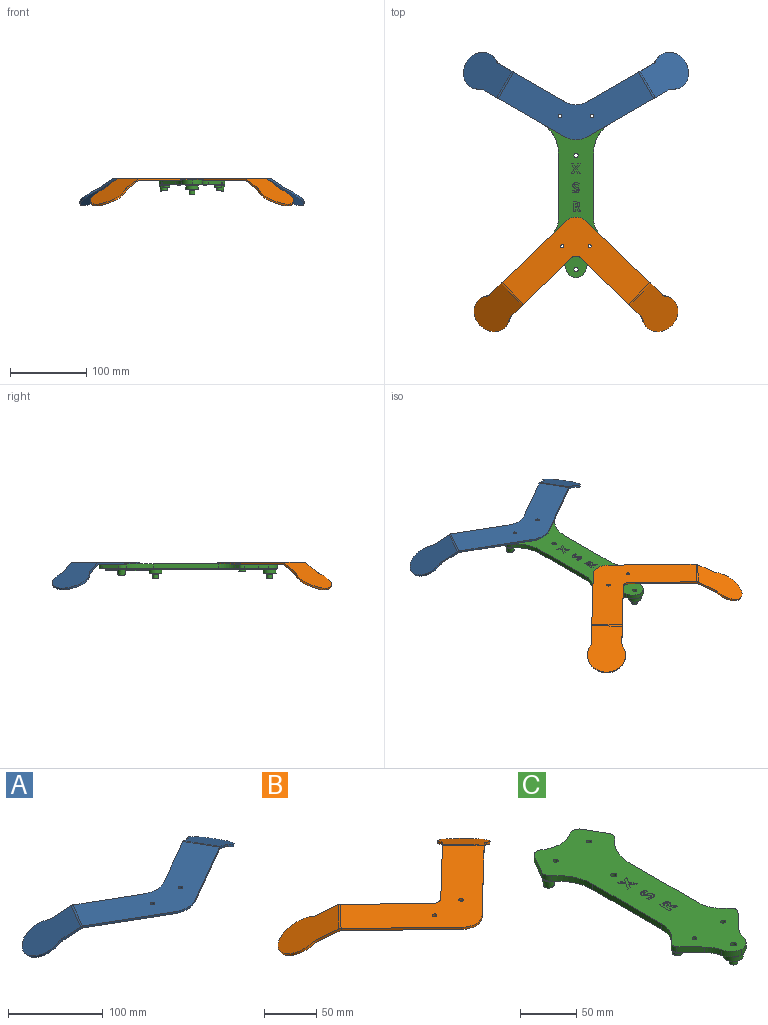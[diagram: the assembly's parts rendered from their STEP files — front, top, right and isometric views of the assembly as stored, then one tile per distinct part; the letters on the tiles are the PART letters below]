
ASSEMBLY  parts=3 mates=2
PART A: 32 faces, bbox 296.1x115.1x36.2 mm
  f0: plane 67.21x38.81mm, normal (0.5,0.87,0), area 194mm2, adj f6,f7,f9,f29
  f1: plane 67.21x38.81mm, normal (-0.5,0.87,0), area 194mm2, adj f6,f7,f9,f17
  f2: plane 87.21x50.35mm, normal (0.5,-0.87,0), area 251.8mm2, adj f6,f7,f8,f18
  f3: cylinder r=2.15mm len=4.3mm, axis (0,0,1), area 33.8mm2, adj f6,f7
  f4: cylinder r=2.15mm len=4.3mm, axis (0,0,1), area 33.8mm2, adj f6,f7
  f5: plane 87.21x50.35mm, normal (-0.5,-0.87,0), area 251.8mm2, adj f6,f7,f8,f28
  f6: plane 204.42x89.01mm, normal (0,0,-1), area 8489.2mm2, adj f0,f1,f2,f3,f4,f5,f8,f9
  f7: plane 204.42x89.01mm, normal (0,0,1), area 8489.2mm2, adj f0,f1,f2,f3,f4,f5,f8,f9
  f8: cylinder r=30mm len=30mm, axis (0,0,1), area 78.5mm2, adj f2,f5,f6,f7
  f9: cylinder r=30mm len=30mm, axis (0,0,-1), area 78.5mm2, adj f0,f1,f6,f7
  f10: plane 18.92x14.06mm, normal (0.5,-0.87,0), area 59.4mm2, adj f13,f14,f15,f18
  f11: plane 18.92x14.06mm, normal (-0.5,0.87,0), area 59.4mm2, adj f13,f14,f16,f17
  f12: cylinder r=25mm len=49.04mm, axis (-0.43,-0.25,-0.87), area 264mm2, adj f13,f14,f15,f16
  f13: plane 63.89x59.63mm, normal (-0.43,-0.25,-0.87), area 2757.9mm2, adj f10,f11,f12,f15,f16,f20
  f14: plane 63.89x59.63mm, normal (0.43,0.25,0.87), area 2757.9mm2, adj f10,f11,f12,f15,f16,f19
  f15: cylinder r=10mm len=5.66mm, axis (-0.43,-0.25,-0.87), area 13.5mm2, adj f10,f12,f13,f14
  f16: cylinder r=10mm len=4.74mm, axis (-0.43,-0.25,-0.87), area 13.5mm2, adj f11,f12,f13,f14
  f17: plane 2.76x1.93mm, normal (-0.5,0.87,0), area 4.2mm2, adj f1,f11,f19,f20
  f18: plane 2.76x1.93mm, normal (0.5,-0.87,0), area 4.2mm2, adj f2,f10,f19,f20
  f19: cylinder r=4.45mm len=35.75mm, axis (-0.5,0.87,0), area 93.2mm2, adj f7,f14,f17,f18
  f20: cylinder r=1.95mm len=35.13mm, axis (-0.5,0.87,0), area 40.8mm2, adj f6,f13,f17,f18
  f21: plane 18.92x14.06mm, normal (0.5,0.87,0), area 59.4mm2, adj f24,f25,f26,f29
  f22: plane 18.92x14.06mm, normal (-0.5,-0.87,0), area 59.4mm2, adj f24,f25,f27,f28
  f23: cylinder r=25mm len=49.04mm, axis (0.43,-0.25,-0.87), area 264mm2, adj f24,f25,f26,f27
  f24: plane 63.89x59.63mm, normal (0.43,-0.25,-0.87), area 2757.9mm2, adj f21,f22,f23,f26,f27,f31
  f25: plane 63.89x59.63mm, normal (-0.43,0.25,0.87), area 2757.9mm2, adj f21,f22,f23,f26,f27,f30
  f26: cylinder r=10mm len=4.74mm, axis (0.43,-0.25,-0.87), area 13.5mm2, adj f21,f23,f24,f25
  f27: cylinder r=10mm len=5.66mm, axis (0.43,-0.25,-0.87), area 13.5mm2, adj f22,f23,f24,f25
  f28: plane 2.76x1.93mm, normal (-0.5,-0.87,0), area 4.2mm2, adj f5,f22,f30,f31
  f29: plane 2.76x1.93mm, normal (0.5,0.87,0), area 4.2mm2, adj f0,f21,f30,f31
  f30: cylinder r=4.45mm len=35.75mm, axis (-0.5,-0.87,0), area 93.2mm2, adj f7,f25,f28,f29
  f31: cylinder r=1.95mm len=35.13mm, axis (-0.5,-0.87,0), area 40.8mm2, adj f6,f24,f28,f29
PART B: 32 faces, bbox 268.1x150.4x36.2 mm
  f0: plane 63.62x61.43mm, normal (0.69,0.72,0), area 221.1mm2, adj f6,f7,f9,f29
  f1: plane 63.62x61.43mm, normal (-0.69,0.72,0), area 221.1mm2, adj f6,f7,f9,f17
  f2: plane 83.07x80.22mm, normal (0.69,-0.72,0), area 288.7mm2, adj f6,f7,f8,f18
  f3: cylinder r=2.15mm len=4.3mm, axis (0,0,1), area 33.8mm2, adj f6,f7
  f4: cylinder r=2.15mm len=4.3mm, axis (0,0,1), area 33.8mm2, adj f6,f7
  f5: plane 83.07x80.22mm, normal (-0.69,-0.72,0), area 288.7mm2, adj f6,f7,f8,f28
  f6: plane 193.92x114.6mm, normal (0,0,-1), area 9142.7mm2, adj f0,f1,f2,f3,f4,f5,f8,f9
  f7: plane 193.92x114.6mm, normal (0,0,1), area 9142.7mm2, adj f0,f1,f2,f3,f4,f5,f8,f9
  f8: cylinder r=20mm len=27.79mm, axis (0,0,1), area 76.8mm2, adj f2,f5,f6,f7
  f9: cylinder r=8mm len=11.11mm, axis (0,0,-1), area 30.7mm2, adj f0,f1,f6,f7
  f10: plane 15.71x15.17mm, normal (0.69,-0.72,0), area 59.4mm2, adj f13,f14,f15,f18
  f11: plane 15.71x15.17mm, normal (-0.69,0.72,0), area 59.4mm2, adj f13,f14,f16,f17
  f12: cylinder r=25mm len=47.47mm, axis (-0.36,-0.35,-0.87), area 264mm2, adj f13,f14,f15,f16
  f13: plane 63.27x62.98mm, normal (-0.36,-0.35,-0.87), area 2757.9mm2, adj f10,f11,f12,f15,f16,f20
  f14: plane 63.27x62.98mm, normal (0.36,0.35,0.87), area 2757.9mm2, adj f10,f11,f12,f15,f16,f19
  f15: cylinder r=10mm len=5.1mm, axis (-0.36,-0.35,-0.87), area 13.5mm2, adj f10,f12,f13,f14
  f16: cylinder r=10mm len=4.99mm, axis (-0.36,-0.35,-0.87), area 13.5mm2, adj f11,f12,f13,f14
  f17: plane 2.76x1.6mm, normal (-0.69,0.72,0), area 4.2mm2, adj f1,f11,f19,f20
  f18: plane 2.76x1.6mm, normal (0.69,-0.72,0), area 4.2mm2, adj f2,f10,f19,f20
  f19: cylinder r=4.45mm len=30.32mm, axis (-0.69,0.72,0), area 93.2mm2, adj f7,f14,f17,f18
  f20: cylinder r=1.95mm len=29.45mm, axis (-0.69,0.72,0), area 40.8mm2, adj f6,f13,f17,f18
  f21: plane 15.71x15.17mm, normal (0.69,0.72,0), area 59.4mm2, adj f24,f25,f26,f29
  f22: plane 15.71x15.17mm, normal (-0.69,-0.72,0), area 59.4mm2, adj f24,f25,f27,f28
  f23: cylinder r=25mm len=47.47mm, axis (0.36,-0.35,-0.87), area 264mm2, adj f24,f25,f26,f27
  f24: plane 63.27x62.98mm, normal (0.36,-0.35,-0.87), area 2757.9mm2, adj f21,f22,f23,f26,f27,f31
  f25: plane 63.27x62.98mm, normal (-0.36,0.35,0.87), area 2757.9mm2, adj f21,f22,f23,f26,f27,f30
  f26: cylinder r=10mm len=4.99mm, axis (0.36,-0.35,-0.87), area 13.5mm2, adj f21,f23,f24,f25
  f27: cylinder r=10mm len=5.1mm, axis (0.36,-0.35,-0.87), area 13.5mm2, adj f22,f23,f24,f25
  f28: plane 2.76x1.6mm, normal (-0.69,-0.72,0), area 4.2mm2, adj f5,f22,f30,f31
  f29: plane 2.76x1.6mm, normal (0.69,0.72,0), area 4.2mm2, adj f0,f21,f30,f31
  f30: cylinder r=4.45mm len=30.32mm, axis (-0.69,-0.72,0), area 93.2mm2, adj f7,f25,f28,f29
  f31: cylinder r=1.95mm len=29.45mm, axis (-0.69,-0.72,0), area 40.8mm2, adj f6,f24,f28,f29
PART C: 179 faces, bbox 86x237.1x20.2 mm
  f0: cylinder r=3.8mm len=8.7mm, axis (0.17,0,-0.98), area 167.1mm2, adj f88,f178
  f1: cylinder r=3.8mm len=8.7mm, axis (-0.17,0,-0.98), area 167.1mm2, adj f90,f177
  f2: plane 234.51x85.78mm, normal (0,0,1), area 11832.9mm2, adj f4,f5,f6,f7,f8,f9,f10,f11
  f3: plane 234.51x81.33mm, normal (0,0,-1), area 6895.4mm2, adj f8,f9,f10,f11,f12,f13,f14,f15
  f4: cylinder r=2.2mm len=4.4mm, axis (0,0,1), area 48.4mm2, adj f2,f54
  f5: cylinder r=2.2mm len=4.4mm, axis (0,0,1), area 48.4mm2, adj f2,f52
  f6: cylinder r=2.2mm len=4.4mm, axis (0,0,1), area 48.4mm2, adj f2,f50
  f7: cylinder r=2.2mm len=4.4mm, axis (0,0,1), area 48.4mm2, adj f2,f48
  f8: plane 21.39x12.39mm, normal (0.87,0.5,0), area 147.6mm2, adj f2,f3,f81,f84,f92
  f9: plane 6x3.59mm, normal (-0.5,0.87,0), area 24.9mm2, adj f2,f3,f38,f81
  f10: plane 6x3.59mm, normal (0.5,0.87,0), area 24.9mm2, adj f2,f3,f38,f82
  f11: plane 21.39x12.38mm, normal (-0.87,0.5,0), area 147.6mm2, adj f2,f3,f82,f83,f99
  f12: plane 86.29x6mm, normal (-1,0,0), area 517.7mm2, adj f2,f3,f43,f79
  f13: plane 6.25x6.19mm, normal (-0.69,0.72,0), area 49.6mm2, adj f2,f3,f43,f45,f100
  f14: plane 17.96x17.35mm, normal (-0.72,-0.69,0), area 147.7mm2, adj f2,f3,f41,f45,f103
  f15: plane 17.96x17.35mm, normal (0.72,-0.69,0), area 147.7mm2, adj f2,f3,f42,f46,f104
  f16: plane 6.25x6.19mm, normal (0.69,0.72,0), area 49.6mm2, adj f2,f3,f44,f46,f107
  f17: plane 86.29x6mm, normal (1,0,0), area 517.7mm2, adj f2,f3,f44,f80
  f18: cylinder r=8.5mm len=17mm, axis (0,0,1), area 263mm2, adj f19,f56,f68,f74,f85,f86,f87
  f19: plane 17x17mm, normal (0,0,-1), area 170.2mm2, adj f18,f175
  f20: cylinder r=8.5mm len=17mm, axis (0,0,1), area 267mm2, adj f21,f56,f73
  f21: plane 17x17mm, normal (0,0,-1), area 170.2mm2, adj f20,f176
  f22: cylinder r=2.75mm len=20mm, axis (0,0,1), area 345.6mm2, adj f2,f172
  f23: cylinder r=2.75mm len=20mm, axis (0,0,1), area 345.6mm2, adj f2,f174
  f24: plane 150x3mm, normal (0,0,-1), area 450mm2, adj f28,f29,f34,f35
  f25: plane 150x3mm, normal (0,0,-1), area 450mm2, adj f26,f27,f36,f37
  f26: plane 150.21x0.64mm, normal (-0.95,0,-0.32), area 100mm2, adj f25,f33,f36,f37
  f27: plane 150.21x0.64mm, normal (0.95,0,-0.32), area 100mm2, adj f25,f32,f36,f37
  f28: plane 150.21x0.64mm, normal (-0.95,0,-0.32), area 100mm2, adj f24,f31,f34,f35
  f29: plane 150.21x0.64mm, normal (0.95,0,-0.32), area 100mm2, adj f24,f30,f34,f35
  f30: cylinder r=2mm len=154mm, axis (0,1,0), area 380mm2, adj f3,f29,f34,f35
  f31: cylinder r=2mm len=154mm, axis (0,1,0), area 380mm2, adj f3,f28,f34,f35
  f32: cylinder r=2mm len=154mm, axis (0,1,0), area 380mm2, adj f3,f27,f36,f37
  f33: cylinder r=2mm len=154mm, axis (0,1,0), area 380mm2, adj f3,f26,f36,f37
  f34: cylinder r=2mm len=7.22mm, axis (-1,0,0), area 15.4mm2, adj f3,f24,f28,f29,f30,f31
  f35: cylinder r=2mm len=7.22mm, axis (1,0,0), area 15.4mm2, adj f3,f24,f28,f29,f30,f31
  f36: cylinder r=2mm len=7.22mm, axis (-1,0,0), area 15.4mm2, adj f3,f25,f26,f27,f32,f33
  f37: cylinder r=2mm len=7.22mm, axis (1,0,0), area 15.4mm2, adj f3,f25,f26,f27,f32,f33
  f38: cylinder r=30mm len=30mm, axis (0,0,-1), area 188.5mm2, adj f2,f3,f9,f10
  f39: cylinder r=15mm len=13.51mm, axis (0,0,-1), area 113.9mm2, adj f2,f3,f40,f42
  f40: cylinder r=15mm len=13.51mm, axis (0,0,-1), area 113.9mm2, adj f2,f3,f39,f41
  f41: cylinder r=30mm len=13.92mm, axis (0,0,-1), area 96.3mm2, adj f2,f3,f14,f40
  f42: cylinder r=30mm len=13.92mm, axis (0,0,-1), area 96.3mm2, adj f2,f3,f15,f39
  f43: cylinder r=30mm len=21.58mm, axis (0,0,1), area 144.5mm2, adj f2,f3,f12,f13
  f44: cylinder r=30mm len=21.58mm, axis (0,0,1), area 144.5mm2, adj f2,f3,f16,f17
  f45: cylinder r=5mm len=7.07mm, axis (0,0,-1), area 47.1mm2, adj f2,f13,f14,f102
  f46: cylinder r=5mm len=7.07mm, axis (0,0,-1), area 47.1mm2, adj f2,f15,f16,f106
  f47: cylinder r=5mm len=10mm, axis (0,0,-1), area 78.5mm2, adj f3,f48
  f48: plane 10x10mm, normal (0,0,-1), area 63.3mm2, adj f7,f47
  f49: cylinder r=5mm len=10mm, axis (0,0,-1), area 78.5mm2, adj f3,f50
  f50: plane 10x10mm, normal (0,0,-1), area 63.3mm2, adj f6,f49
  f51: cylinder r=5mm len=10mm, axis (0,0,-1), area 78.5mm2, adj f3,f52
  f52: plane 10x10mm, normal (0,0,-1), area 63.3mm2, adj f5,f51
  f53: cylinder r=5mm len=10mm, axis (0,0,-1), area 78.5mm2, adj f3,f54
  f54: plane 10x10mm, normal (0,0,-1), area 63.3mm2, adj f4,f53
  f55: plane 4.54x2mm, normal (0,1,0), area 8.2mm2, adj f67,f72,f78,f85,f86,f87
  f56: plane 133.48x9.6mm, normal (0,0,-1), area 522.4mm2, adj f18,f20,f65,f69,f70,f71,f75,f76
  f57: cylinder r=3.8mm len=7.6mm, axis (0,0,1), area 95.5mm2, adj f59,f60
  f58: cylinder r=4.8mm len=9.6mm, axis (0,0,1), area 65.6mm2, adj f59,f104,f105,f106,f107
  f59: plane 9.6x9.6mm, normal (0,0,-1), area 27mm2, adj f57,f58
  f60: plane 7.6x7.6mm, normal (0,0,-1), area 45.4mm2, adj f57
  f61: cylinder r=3.8mm len=7.6mm, axis (0,0,1), area 95.5mm2, adj f63,f64
  f62: cylinder r=4.8mm len=9.6mm, axis (0,0,1), area 65.6mm2, adj f63,f100,f101,f102,f103
  f63: plane 9.6x9.6mm, normal (0,0,-1), area 27mm2, adj f61,f62
  f64: plane 7.6x7.6mm, normal (0,0,-1), area 45.4mm2, adj f61
  f65: cylinder r=3.8mm len=7.6mm, axis (0,0,1), area 47.8mm2, adj f56,f66
  f66: plane 7.6x7.6mm, normal (0,0,-1), area 45.4mm2, adj f65
  f67: cylinder r=2mm len=58.39mm, axis (0,1,0), area 179.1mm2, adj f3,f55,f68,f78,f86
  f68: torus R=10.5mm, axis (0,0,1), area 72.7mm2, adj f3,f18,f67,f69
  f69: cylinder r=2mm len=44.63mm, axis (0,1,0), area 136.1mm2, adj f3,f56,f68,f70
  f70: torus R=6.8mm, axis (0,0,1), area 35.9mm2, adj f3,f56,f69,f71
  f71: cylinder r=2mm len=80.13mm, axis (0,1,0), area 247.7mm2, adj f3,f56,f70,f73
  f72: cylinder r=2mm len=58.39mm, axis (0,-1,0), area 179.1mm2, adj f3,f55,f74,f78,f85
  f73: torus R=10.5mm, axis (0,0,1), area 163.7mm2, adj f3,f20,f71,f75
  f74: torus R=10.5mm, axis (0,0,1), area 72.7mm2, adj f3,f18,f72,f76
  f75: cylinder r=2mm len=80.13mm, axis (0,-1,0), area 247.7mm2, adj f3,f56,f73,f77
  f76: cylinder r=2mm len=44.63mm, axis (0,-1,0), area 136.1mm2, adj f3,f56,f74,f77
  f77: torus R=6.8mm, axis (0,0,1), area 35.9mm2, adj f3,f56,f75,f76
  f78: cylinder r=1mm len=8mm, axis (-1,0,0), area 9.8mm2, adj f3,f55,f67,f72
  f79: cylinder r=45mm len=35.14mm, axis (0,0,-1), area 241.9mm2, adj f2,f3,f12,f83,f96
  f80: cylinder r=45mm len=35.14mm, axis (0,0,-1), area 241.9mm2, adj f2,f3,f17,f84,f95
  f81: cylinder r=8mm len=10.93mm, axis (0,0,-1), area 75.4mm2, adj f2,f3,f8,f9
  f82: cylinder r=8mm len=10.93mm, axis (0,0,-1), area 75.4mm2, adj f2,f3,f10,f11
  f83: cylinder r=8mm len=10.25mm, axis (0,0,-1), area 68.1mm2, adj f2,f11,f79,f98
  f84: cylinder r=8mm len=10.25mm, axis (0,0,-1), area 68.1mm2, adj f2,f8,f80,f94
  f85: plane 57.39x1mm, normal (-1,0,0), area 57.4mm2, adj f18,f55,f72,f87
  f86: plane 57.39x1mm, normal (1,0,0), area 57.4mm2, adj f18,f55,f67,f87
  f87: plane 57.39x4mm, normal (0,0,-1), area 228.9mm2, adj f18,f55,f85,f86
  f88: plane 9.6x9.46mm, normal (0.17,0,-0.98), area 27mm2, adj f0,f89
  f89: bspline ~10.99x9.6mm, area 198.9mm2, adj f88,f96,f97,f98,f99
  f90: plane 9.6x9.46mm, normal (-0.17,0,-0.98), area 27mm2, adj f1,f91
  f91: bspline ~10.99x9.6mm, area 197mm2, adj f90,f92,f93,f94,f95
  f92: bspline ~3.38x2.53mm, area 4.4mm2, adj f8,f91,f93,f94
  f93: bspline ~13.61x10.48mm, area 70.5mm2, adj f3,f91,f92,f95
  f94: bspline ~11.34x4.44mm, area 13.8mm2, adj f84,f91,f92,f95
  f95: bspline ~2.51x2.1mm, area 1.6mm2, adj f80,f91,f93,f94
  f96: bspline ~2.28x1.98mm, area 1.6mm2, adj f79,f89,f97,f98
  f97: bspline ~13.6x9.87mm, area 70.5mm2, adj f3,f89,f96,f99
  f98: bspline ~11.13x4.2mm, area 13.8mm2, adj f83,f89,f96,f99
  f99: bspline ~3.62x2.75mm, area 4.4mm2, adj f11,f89,f97,f98
  f100: bspline ~4.33x4.25mm, area 7.9mm2, adj f13,f62,f101,f102
  f101: torus R=6.8mm, axis (0,0,1), area 59.5mm2, adj f3,f62,f100,f103
  f102: bspline ~8.29x2.77mm, area 13.1mm2, adj f45,f62,f100,f103
  f103: bspline ~4.13x4.01mm, area 7.9mm2, adj f14,f62,f101,f102
  f104: bspline ~4.36x4.27mm, area 7.9mm2, adj f15,f58,f105,f106
  f105: torus R=6.8mm, axis (0,0,1), area 59.5mm2, adj f3,f58,f104,f107
  f106: bspline ~8.29x2.65mm, area 13.1mm2, adj f46,f58,f104,f107
  f107: bspline ~4.06x4.02mm, area 7.9mm2, adj f16,f58,f105,f106
  f108: plane 4.95x0.5mm, normal (-1,0,0), area 2.5mm2, adj f2,f109,f126,f127
  f109: plane 1.45x0.5mm, normal (0,1,0), area 0.7mm2, adj f2,f108,f110,f127
  f110: plane 4.95x3.08mm, normal (0.85,0.53,0), area 2.9mm2, adj f2,f109,f111,f127
  f111: plane 3.03x0.5mm, normal (0,1,0), area 1.5mm2, adj f2,f110,f112,f127
  f112: extruded ~5.62x3.79mm, area 3.4mm2, adj f2,f111,f113,f127
  f113: extruded ~1.77x1.39mm, area 1.1mm2, adj f2,f112,f114,f127
  f114: extruded ~2.02x0.63mm, area 1.1mm2, adj f2,f113,f115,f127
  f115: extruded ~2.91x1.26mm, area 1.6mm2, adj f2,f114,f116,f127
  f116: extruded ~3.89x0.96mm, area 2mm2, adj f2,f115,f117,f127
  f117: plane 3.76x0.5mm, normal (0,-1,0), area 1.9mm2, adj f2,f116,f118,f127
  f118: plane 12.89x0.5mm, normal (1,0,0), area 6.4mm2, adj f2,f117,f126,f127
  f119: plane 0.88x0.5mm, normal (0,-1,0), area 0.4mm2, adj f120,f125,f127,f128
  f120: plane 3.48x0.5mm, normal (-1,0,0), area 1.7mm2, adj f119,f121,f127,f128
  f121: plane 0.83x0.5mm, normal (0,1,0), area 0.4mm2, adj f120,f122,f127,f128
  f122: extruded ~1.95x0.5mm, area 1mm2, adj f121,f123,f127,f128
  f123: extruded ~1.3x0.63mm, area 0.8mm2, adj f122,f124,f127,f128
  f124: extruded ~1.36x0.62mm, area 0.8mm2, adj f123,f125,f127,f128
  f125: extruded ~1.91x0.5mm, area 1mm2, adj f119,f124,f127,f128
  f126: plane 2.73x0.5mm, normal (0,1,0), area 1.4mm2, adj f2,f108,f118,f127
  f127: plane 12.89x10.3mm, normal (0,0,1), area 81.1mm2, adj f108,f109,f110,f111,f112,f113,f114,f115
  f128: plane 3.48x3.41mm, normal (0,0,1), area 10.5mm2, adj f119,f120,f121,f122,f123,f124,f125
  f129: extruded ~2.75x1.26mm, area 1.6mm2, adj f2,f130,f156,f157
  f130: extruded ~2.13x0.67mm, area 1.1mm2, adj f2,f129,f131,f157
  f131: extruded ~2.48x1.73mm, area 1.5mm2, adj f2,f130,f132,f157
  f132: extruded ~1.73x0.9mm, area 1mm2, adj f2,f131,f133,f157
  f133: extruded ~0.53x0.52mm, area 0.4mm2, adj f2,f132,f134,f157
  f134: extruded ~0.63x0.5mm, area 0.3mm2, adj f2,f133,f135,f157
  f135: extruded ~0.94x0.5mm, area 0.5mm2, adj f2,f134,f136,f157
  f136: extruded ~1.19x0.5mm, area 0.6mm2, adj f2,f135,f137,f157
  f137: extruded ~1.33x0.5mm, area 0.7mm2, adj f2,f136,f138,f157
  f138: extruded ~1.71x0.59mm, area 0.9mm2, adj f2,f137,f139,f157
  f139: plane 2.13x0.88mm, normal (-0.92,0.38,0), area 1.2mm2, adj f2,f138,f140,f157
  f140: extruded ~1.91x0.67mm, area 1mm2, adj f2,f139,f141,f157
  f141: extruded ~1.92x0.5mm, area 1mm2, adj f2,f140,f142,f157
  f142: extruded ~3.21x0.98mm, area 1.7mm2, adj f2,f141,f143,f157
  f143: extruded ~2.69x1.16mm, area 1.5mm2, adj f2,f142,f144,f157
  f144: extruded ~1.59x0.5mm, area 0.8mm2, adj f2,f143,f145,f157
  f145: extruded ~1.19x0.94mm, area 0.8mm2, adj f2,f144,f146,f157
  f146: extruded ~1.77x1.07mm, area 1mm2, adj f2,f145,f147,f157
  f147: extruded ~1.67x0.87mm, area 0.9mm2, adj f2,f146,f148,f157
  f148: extruded ~0.62x0.57mm, area 0.4mm2, adj f2,f147,f149,f157
  f149: extruded ~0.67x0.5mm, area 0.4mm2, adj f2,f148,f150,f157
  f150: extruded ~1.02x0.5mm, area 0.6mm2, adj f2,f149,f151,f157
  f151: extruded ~1.38x0.5mm, area 0.7mm2, adj f2,f150,f152,f157
  f152: extruded ~1.65x0.5mm, area 0.8mm2, adj f2,f151,f153,f157
  f153: extruded ~2.21x0.82mm, area 1.2mm2, adj f2,f152,f154,f157
  f154: plane 2.54x0.5mm, normal (1,0,0), area 1.3mm2, adj f2,f153,f155,f157
  f155: extruded ~3.65x0.78mm, area 1.9mm2, adj f2,f154,f156,f157
  f156: extruded ~3.49x1.01mm, area 1.9mm2, adj f2,f129,f155,f157
  f157: plane 13.25x8.4mm, normal (0,0,1), area 62.7mm2, adj f129,f130,f131,f132,f133,f134,f135,f136
  f158: plane 3.12x0.5mm, normal (0,1,0), area 1.6mm2, adj f2,f159,f169,f170
  f159: plane 6.5x4.36mm, normal (-0.83,-0.56,0), area 3.9mm2, adj f2,f158,f160,f170
  f160: plane 6.39x4.05mm, normal (-0.85,0.53,0), area 3.8mm2, adj f2,f159,f161,f170
  f161: plane 2.94x0.5mm, normal (0,-1,0), area 1.5mm2, adj f2,f160,f162,f170
  f162: plane 4.64x2.73mm, normal (0.86,-0.51,0), area 2.7mm2, adj f2,f161,f163,f170
  f163: plane 4.64x2.78mm, normal (-0.86,-0.51,0), area 2.7mm2, adj f2,f162,f164,f170
  f164: plane 3.02x0.5mm, normal (0,-1,0), area 1.5mm2, adj f2,f163,f165,f170
  f165: plane 6.24x4mm, normal (0.84,0.54,0), area 3.7mm2, adj f2,f164,f166,f170
  f166: plane 6.65x4.28mm, normal (0.84,-0.54,0), area 4mm2, adj f2,f165,f167,f170
  f167: plane 2.93x0.5mm, normal (0,1,0), area 1.5mm2, adj f2,f166,f168,f170
  f168: plane 4.88x3mm, normal (-0.85,0.52,0), area 2.9mm2, adj f2,f167,f169,f170
  f169: plane 4.88x3mm, normal (0.85,0.52,0), area 2.9mm2, adj f2,f158,f168,f170
  f170: plane 12.89x12.04mm, normal (0,0,1), area 70.4mm2, adj f158,f159,f160,f161,f162,f163,f164,f165
  f171: cylinder r=3.75mm len=7.5mm, axis (0,0,1), area 153.2mm2, adj f172,f176
  f172: plane 7.5x7.5mm, normal (0,0,-1), area 20.4mm2, adj f22,f171
  f173: cylinder r=3.75mm len=7.5mm, axis (0,0,1), area 153.2mm2, adj f174,f175
  f174: plane 7.5x7.5mm, normal (0,0,-1), area 20.4mm2, adj f23,f173
  f175: torus R=4.25mm, axis (0,0,-1), area 19.4mm2, adj f19,f173
  f176: torus R=4.25mm, axis (0,0,-1), area 19.4mm2, adj f21,f171
  f177: plane 7.6x7.48mm, normal (-0.17,0,-0.98), area 45.4mm2, adj f1
  f178: plane 7.6x7.48mm, normal (0.17,0,-0.98), area 45.4mm2, adj f0
PLACE A t=(0,72.99,5.5)mm
PLACE B rot(axis=(0,0,1),180deg) t=(0,-67.33,5.5)mm
PLACE C at identity
MATE cylindrical A.f4 <-> C.f4  axis (0,0,-1) through (21,85.74,5.5)mm
MATE slider B.f4 <-> C.f7  axis (0,0,-1) through (18,-85.26,5.5)mm
